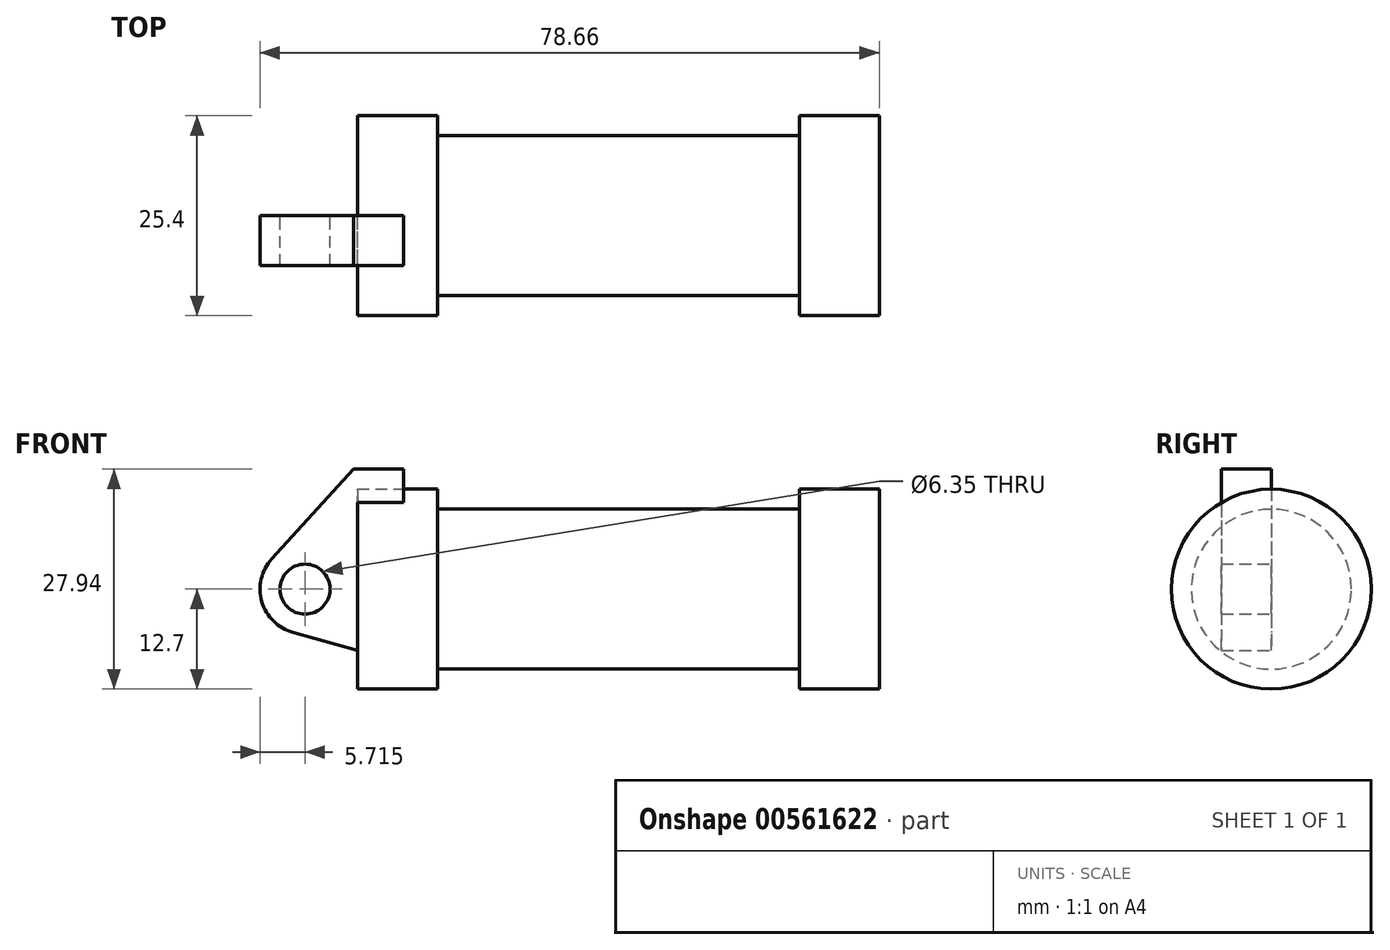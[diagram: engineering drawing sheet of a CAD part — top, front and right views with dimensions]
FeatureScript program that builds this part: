
annotation { "Feature Type Name" : "Feature", "Feature Type Description" : "" }
export const myFeature = defineFeature(function(context is Context, id is Id, definition is map)
    precondition{}
    {
        {
            var Q0;
            Q0=qCreatedBy(makeId("Front.planeOp"),FACE);
            var sketch = newSketch(context, id + "F0", { "sketchPlane" : qUnion([Q0])});
            skLineSegment(sketch, "E0", {"start": v(0, 0) * mm, "end": v(0, 12.7) * mm});
            skLineSegment(sketch, "E1", {"start": v(0, 12.7) * mm, "end": v(10.16, 12.7) * mm});
            skLineSegment(sketch, "E2", {"start": v(10.16, 12.7) * mm, "end": v(10.16, 10.16) * mm});
            skLineSegment(sketch, "E3", {"start": v(10.16, 10.16) * mm, "end": v(56.13, 10.16) * mm});
            skLineSegment(sketch, "E4", {"start": v(56.13, 10.16) * mm, "end": v(56.13, 12.7) * mm});
            skLineSegment(sketch, "E5", {"start": v(56.13, 12.7) * mm, "end": v(66.3, 12.7) * mm});
            skLineSegment(sketch, "E6", {"start": v(66.3, 12.7) * mm, "end": v(66.3, 0) * mm});
            skLineSegment(sketch, "E7", {"start": v(66.3, 0) * mm, "end": v(0, 0) * mm});
            skLineSegment(sketch, "E8", {"start": v(5.84, 15.24) * mm, "end": v(-0.5, 15.24) * mm});
            skLineSegment(sketch, "E9", {"start": v(-0.5, 15.24) * mm, "end": v(-10.88, 3.85) * mm});
            skLineSegment(sketch, "E10", {"start": v(0, 0) * mm, "end": v(-6.65, 0) * mm});
            skCircle(sketch, "E11", {"center": v(-6.65, 0) * mm, "radius": 5.72 * mm});
            skCircle(sketch, "E12", {"center": v(-6.65, 0) * mm, "radius": 3.18 * mm});
            skLineSegment(sketch, "E13", {"start": v(5.84, 15.24) * mm, "end": v(5.84, -9.4) * mm});
            skLineSegment(sketch, "E14", {"start": v(5.84, -9.4) * mm, "end": v(-8.18, -5.5) * mm});
            skSolve(sketch);
        }
        {
            var Q0;
            {var subQ0=sQuery(id+"F0.wireOp",EDGE,"E2");Q0=makeQuery(id+"F0.imprint","IMPRINT",FACE,{"disambiguationData":[TD([[makeQuery(id+"F0.imprint","IMPRINT",EDGE,{"derivedFrom":subQ0}),-1.0]])]});}
            var Q1;
            {var subQ0=sQuery(id+"F0.wireOp",EDGE,"E0");Q1=makeQuery(id+"F0.imprint","IMPRINT",FACE,{"disambiguationData":[TD([[makeQuery(id+"F0.imprint","IMPRINT",EDGE,{"derivedFrom":subQ0}),-1.0]])]});}
            var Q2;
            Q2=sQuery(id+"F0.wireOp",EDGE,"E7");
            revolve(context, id + "F1", {"entities" : qUnion([Q0, Q1]), "axis" : qUnion([Q2]), "revolveType" : RevolveType.FULL});
        }
        {
            var Q0;
            {var subQ5=sQuery(id+"F0.wireOp",EDGE,"E12");Q0=makeQuery(id+"F0.imprint","IMPRINT",FACE,{"disambiguationData":[TD([[makeQuery(id+"F0.imprint","IMPRINT",EDGE,{"derivedFrom":subQ5}),-1.0]])]});}
            var Q1;
            {var subQ1=sQuery(id+"F0.wireOp",EDGE,"E0");Q1=makeQuery(id+"F0.imprint","IMPRINT",FACE,{"disambiguationData":[TD([[makeQuery(id+"F0.imprint","IMPRINT",EDGE,{"derivedFrom":subQ1}),1.0]])]});}
            var Q2;
            {var subQ0=sQuery(id+"F0.wireOp",EDGE,"E14");Q2=makeQuery(id+"F0.imprint","IMPRINT",FACE,{"disambiguationData":[TD([[makeQuery(id+"F0.imprint","IMPRINT",EDGE,{"derivedFrom":subQ0}),-1.0]])]});}
            var Q3;
            {var subQ0=sQuery(id+"F0.wireOp",EDGE,"E0");Q3=makeQuery(id+"F0.imprint","IMPRINT",FACE,{"disambiguationData":[TD([[makeQuery(id+"F0.imprint","IMPRINT",EDGE,{"derivedFrom":subQ0}),-1.0]])]});}
            extrude(context, id + "F2", {"entities" : qUnion([Q0, Q1, Q2, Q3]), "operationType" : NewBodyOperationType.ADD, "depth" : 6.35 * mm, "offsetDistance" : 25.4 * mm});
        }
    });
